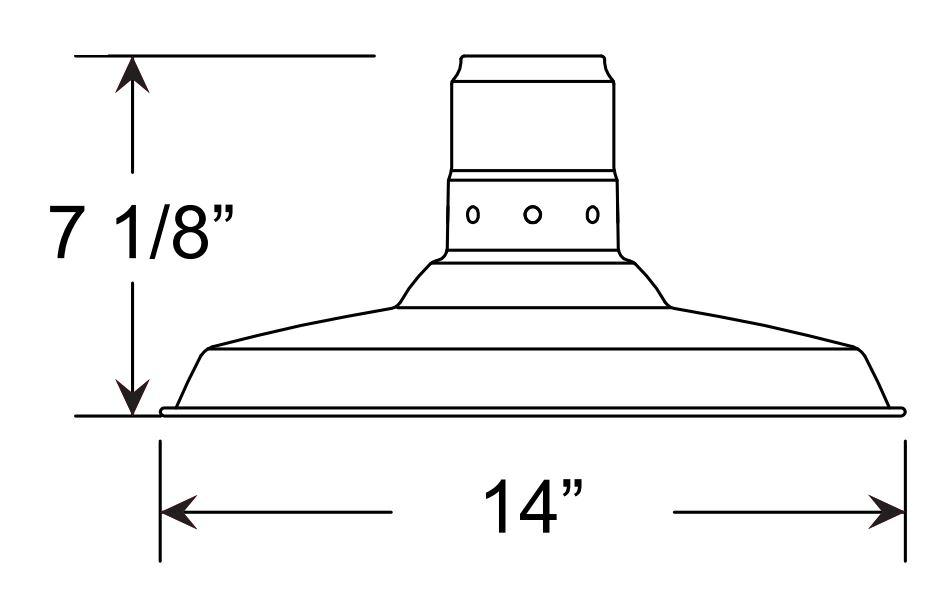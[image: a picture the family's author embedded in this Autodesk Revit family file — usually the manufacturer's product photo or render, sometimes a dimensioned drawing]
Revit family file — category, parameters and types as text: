
# Revit family: Urban Bistro BRU 14,16,18,20,22
name_source: partatom
category: Lighting Fixtures
units: mm (PartAtom-declared; Revit-internal decimal feet)

## family parameters
Always vertical = Yes
Cut with Voids When Loaded = No
Light Source = Yes
OmniClass Number = 23.80.70.00
OmniClass Title = Lighting
Part Type = Normal
Room Calculation Point = No
Round Connector Dimension = Use Diameter
Shared = No
Work Plane-Based = No

## types (5) — shared parameters
Apparent Load = 200 VA
Body Colour = Spun aluminium
Body Material = Putty
CRI = >90
Canopy Body = Aqua Green
Color Filter = 16777215
Construction Material = Heavy Duty spun aluminum.
Default Elevation = 0' - 0"
Description = 120-277 Voltage
Dimming = 1%
Dimming Lamp Color Temperature Shift = <None>
Efficiency = 65-125 lumens per watt
HUB = Putty
Lamp = MB
Life = L70 50,000 hours
Load Classification = Lighting
Manufacturer = ANP Lighting
Photometric Web File = generic
Power Factor = 1
Tilt Angle = 90.00°
URL = https://www.anplighting.com
Voltage = 120 V
Warranty = 5 year limited warranty
Wattage Comments = 200W
b = 0' - 3"

## per-type parameters (varying)
| type | BRU14 | BRU16 | BRU18 | BRU20 | BRU22 | Fixture Diameter | Fixture Height | Weight | a |
| BRU14 | Yes | No | No | No | No | 1' - 2" | 0' - 10" | 3.7lb | 0' - 11" |
| BRU16 | No | Yes | No | No | No | 1' - 4" | 0' - 10 1/2" | 4.2lb | 0' - 11" |
| BRU18 | No | No | Yes | No | No | 1' - 6" | 0' - 10 1/2" | 4.7lb | 0' - 11" |
| BRU20 | No | No | No | Yes | No | 1' - 8 1/4" | 0' - 11" | 5.7lb | 1' - 0" |
| BRU22 | No | No | No | No | Yes | 1' - 10" | 0' - 11 3/4" | 6.2lb | 1' - 1" |

note: column(s) folded — value = type name in every type: Model

## geometry (parser evidence)
native form markers: Sweep x38
no freeform markers — native parametric forms only
